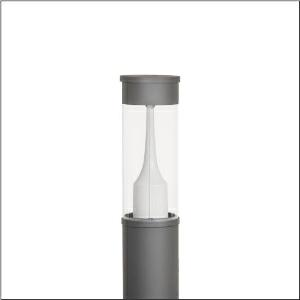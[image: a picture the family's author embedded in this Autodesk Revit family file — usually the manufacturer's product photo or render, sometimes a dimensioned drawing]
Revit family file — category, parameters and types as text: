
# Revit family: city-light_120_iq___p1_0a_5xa5285bf14h_8c15
name_source: partatom
category: Lighting Fixtures
units: mm (PartAtom-declared; Revit-internal decimal feet)

## family parameters
Cut with Voids When Loaded = No
Host = Face
Light Source = No
Part Type = Normal
Room Calculation Point = No
Round Connector Dimension = Use Diameter
Shared = No

## types (1)
- --- (1 x LED, 1510 lm, 12.9 W, 2200K)
    Apparent Load = 13 VA
    CIE Flux Codes = 32 61 90 93 100
    Color Rendering = 70
    Color Temperature = 2200K
    Default Elevation = 1800 mm
    Description = City-Light 120 iQ, bollard luminaire, Module 540 iQ-SR, primary light control with 3 zone facetted reflector, of plastic, silver coated, highly specular, structured, primary optical cover: cover, of PMMA, transparent, partly coated, light distribution: P1.0a, primary light characteristic: strongly asymmetric, LED, High Power LED, rated luminous flux: 1.510lm, luminous efficacy: 117lm/W, light colour: 722, colour temperature: 2200K, control gear: ECG iQ, control: pre-setting: logarithmic dimming characteristic, Street-Remote, Auto-Match, Temp-Guard, Lumen-Switch, Night-Set, Smart-Wire, Light-Fading, Desk-Remote (wireless, voltage-free reading and setting of iQ features in the workshop via application-optimized NFC function/RFID function), optimised constant luminous flux control (CLO 2.0), with terminal, 6-pole, max. 2.5mm², mains connection: 230..240V, AC, 50/60Hz, start of lifetime: 13W, end of service life: 13W, reduction: 6W, luminaire housing, cylindrical, of extruded aluminium section, coated, Siteco® metallic grey (DB 702S), length: 1.200mm, diameter: 200mm, Module 540 iQ-SR, traffic white (RAL 9016), equipment: standard, protection rating (complete): IP54, insulation class (complete): insulation class II (safety insulation), certification: CE, ENEC, VDE, packaging unit: 1 piece

Light Distribution: P1.0a
    Height = 500 mm
    Lamp = 1 x LED
    Lamp Light Flux = 1510 lm
    Lamp Power = 12.9 W
    Lamp count = 1
    Length = 200 mm  [stored 0.656168 ft]
    Luminous efficacy = 117 lm/W
    Manufacturer = Siteco
    ModVariant = No
    Model = 5XA5285BF14H
    Mounting Place = Floor
    Mounting Type = Freestanding
    Number of Poles = 1
    OnlyDefault = Yes
    Power Factor = 1
    Product Name = City-Light 120 iQ | P1.0a
    Product group = bollard luminaire
    ProductGroupID = 1304
    Protection Class = Protection class II
    Protection Degree = IP 54
    RLX_Detail_Level = 1
    RLX_Emergency_Light_Flux = 0 lm
    RLX_Emergency_Type = 0
    RLX_Emergency_Type_DB = No
    RlxData = <blob elided: 52965 chars, md5=1dc0704e>
    Socket = socket
    Standby Power = 0 W
    System Light Flux = 1510 lm
    System Power = 13 W
    Type Comments = factory setting: luminous flux: 100 % | dim-lin: 254 | 516 mA
    Type Image = l_1006922.jpg
    URL = http://relux.com
    VarID = @adj_129985
    Voltage = 0 V
    Weight = 0.00 kg
    Width = 0 mm  [stored 0 ft]

note: [stored X ft] marks values corroborated as IEEE doubles in the binary element streams (Revit-internal decimal feet)

## geometry (parser evidence)
native form markers: Blend x4, Sweep x11
no freeform markers — native parametric forms only
